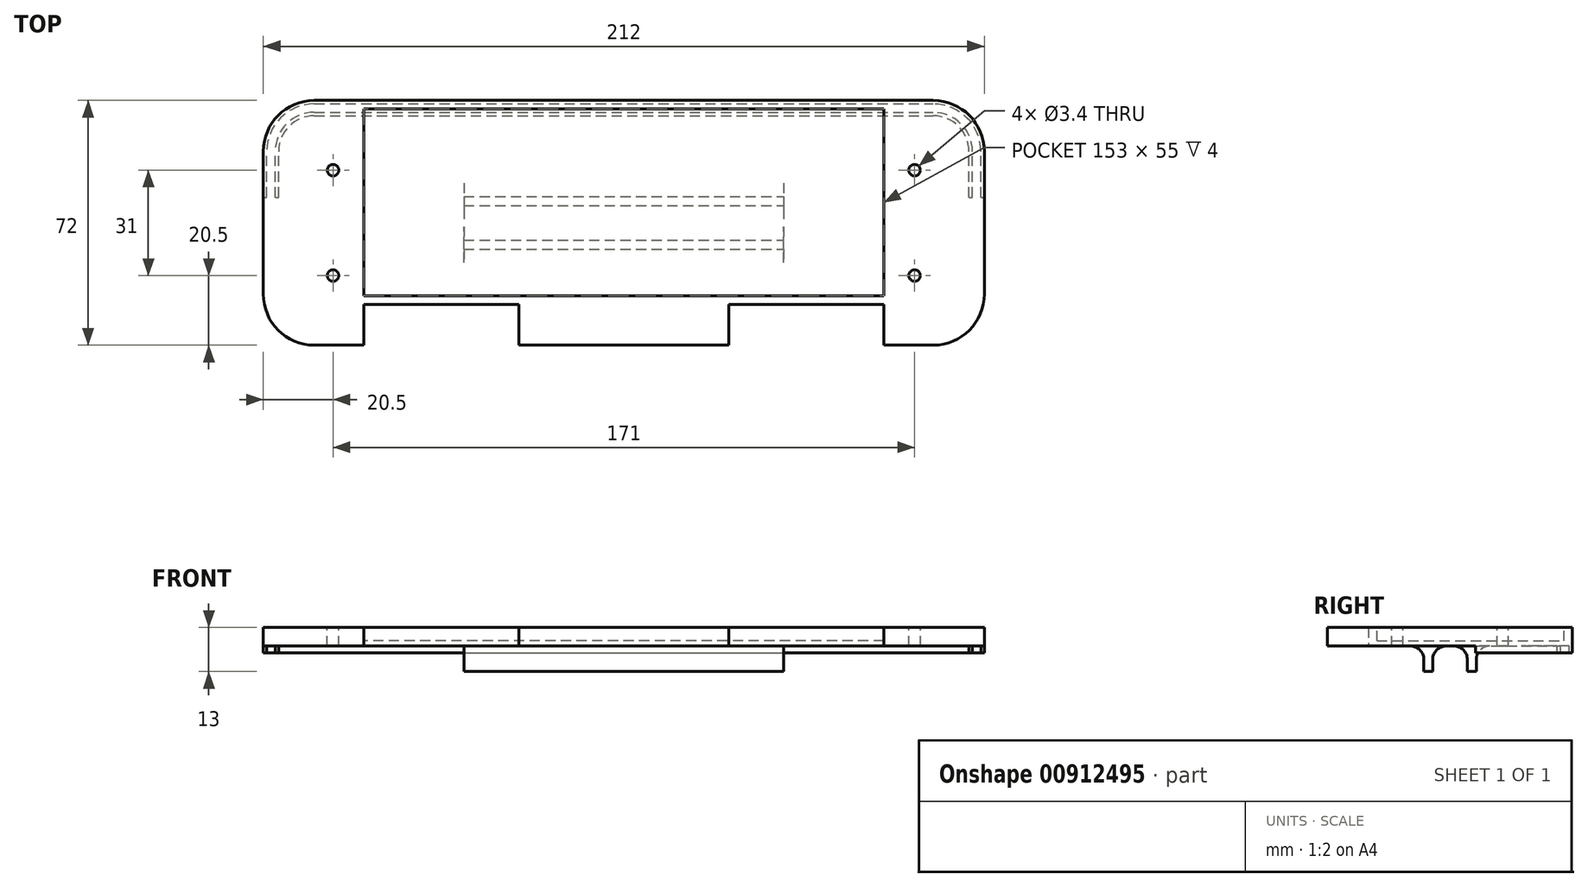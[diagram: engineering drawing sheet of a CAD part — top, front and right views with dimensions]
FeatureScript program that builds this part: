
annotation { "Feature Type Name" : "Feature", "Feature Type Description" : "" }
export const myFeature = defineFeature(function(context is Context, id is Id, definition is map)
    precondition{}
    {
        {
            var Q0;
            Q0=qCreatedBy(makeId("Top.planeOp"),FACE);
            var sketch = newSketch(context, id + "F0", { "sketchPlane" : qUnion([Q0])});
            skLineSegment(sketch, "E0.bottom", {"start": v(-106, 36) * mm, "end": v(106, 36) * mm});
            skLineSegment(sketch, "E0.top", {"start": v(-106, -36) * mm, "end": v(106, -36) * mm});
            skLineSegment(sketch, "E0.left", {"start": v(-106, 36) * mm, "end": v(-106, -36) * mm});
            skLineSegment(sketch, "E0.right", {"start": v(106, 36) * mm, "end": v(106, -36) * mm});
            skPoint(sketch, "E0.middle", {"position": v(0, 0) * mm});
            skSolve(sketch);
        }
        {
            var Q0;
            Q0=qSketchRegion(id+"F0",true);
            extrude(context, id + "F1", {"entities" : qUnion([Q0]), "depth" : 5.5 * mm, "offsetDistance" : 25 * mm});
        }
        {
            var Q0;
            Q0=makeQuery(id+"F1.opExtrude","SWEPT_EDGE",EDGE,{"disambiguationData":[OSD([sQuery(id+"F0.wireOp",EDGE,"E0.top"),sQuery(id+"F0.wireOp",EDGE,"E0.left")])]});
            var Q1;
            Q1=makeQuery(id+"F1.opExtrude","SWEPT_EDGE",EDGE,{"disambiguationData":[OSD([sQuery(id+"F0.wireOp",EDGE,"E0.top"),sQuery(id+"F0.wireOp",EDGE,"E0.right")])]});
            fillet(context, id + "F2", {"entities" : qUnion([Q0, Q1]), "radius" : 15 * mm, "tangentPropagation" : true, "allowEdgeOverflow" : false});
        }
        {
            var Q0;
            Q0=makeQuery(id+"F1.opExtrude","SWEPT_FACE",FACE,{"disambiguationData":[OSD([sQuery(id+"F0.wireOp",EDGE,"E0.top")])]});
            var sketch = newSketch(context, id + "F3", { "sketchPlane" : qUnion([Q0])});
            skLineSegment(sketch, "E1.bottom", {"start": v(-76.5, 5.5) * mm, "end": v(-30.88, 5.5) * mm});
            skLineSegment(sketch, "E1.top", {"start": v(-76.5, 0) * mm, "end": v(-30.88, 0) * mm});
            skLineSegment(sketch, "E1.left", {"start": v(-76.5, 5.5) * mm, "end": v(-76.5, 0) * mm});
            skLineSegment(sketch, "E1.right", {"start": v(-30.88, 5.5) * mm, "end": v(-30.88, 0) * mm});
            skLineSegment(sketch, "E2.bottom", {"start": v(30.88, 5.5) * mm, "end": v(76.5, 5.5) * mm});
            skLineSegment(sketch, "E2.top", {"start": v(30.88, 0) * mm, "end": v(76.5, 0) * mm});
            skLineSegment(sketch, "E2.left", {"start": v(30.88, 5.5) * mm, "end": v(30.88, 0) * mm});
            skLineSegment(sketch, "E2.right", {"start": v(76.5, 5.5) * mm, "end": v(76.5, 0) * mm});
            skSolve(sketch);
        }
        {
            var Q0;
            Q0=qSketchRegion(id+"F3",true);
            extrude(context, id + "F4", {"entities" : qUnion([Q0]), "operationType" : NewBodyOperationType.REMOVE, "oppositeDirection" : true, "depth" : 12 * mm, "offsetDistance" : 25 * mm});
        }
        {
            var Q0;
            Q0=makeQuery(id+"F1.opExtrude","CAP_FACE",FACE,{"disambiguationData":[OSD([sQuery(id+"F0.wireOp",EDGE,"E0.bottom"),sQuery(id+"F0.wireOp",EDGE,"E0.top"),sQuery(id+"F0.wireOp",EDGE,"E0.left"),sQuery(id+"F0.wireOp",EDGE,"E0.right")])],"isStart":true});
            var sketch = newSketch(context, id + "F5", { "sketchPlane" : qUnion([Q0])});
            skLineSegment(sketch, "E3.bottom", {"start": v(-106, -7.5) * mm, "end": v(-105, -7.5) * mm});
            skLineSegment(sketch, "E3.top", {"start": v(-106, -36) * mm, "end": v(106, -36) * mm});
            skLineSegment(sketch, "E3.left", {"start": v(-106, -7.5) * mm, "end": v(-106, -36) * mm});
            skLineSegment(sketch, "E3.right", {"start": v(106, -7.5) * mm, "end": v(106, -36) * mm});
            skLineSegment(sketch, "E4.top", {"start": v(-101.5, -31.5) * mm, "end": v(101.5, -31.5) * mm});
            skLineSegment(sketch, "E4.left", {"start": v(-101.5, -7.5) * mm, "end": v(-101.5, -31.5) * mm});
            skLineSegment(sketch, "E4.right", {"start": v(101.5, -7.5) * mm, "end": v(101.5, -31.5) * mm});
            skLineSegment(sketch, "E5.trimOffspring", {"start": v(101.5, -7.5) * mm, "end": v(102.5, -7.5) * mm});
            skLineSegment(sketch, "E6.bottom", {"start": v(-102.5, -7.5) * mm, "end": v(-101.5, -7.5) * mm});
            skLineSegment(sketch, "E6.top", {"start": v(-105, -35) * mm, "end": v(105, -35) * mm});
            skLineSegment(sketch, "E6.left", {"start": v(-105, -7.5) * mm, "end": v(-105, -35) * mm});
            skLineSegment(sketch, "E6.right", {"start": v(105, -7.5) * mm, "end": v(105, -35) * mm});
            skLineSegment(sketch, "E7.top", {"start": v(-102.5, -32.5) * mm, "end": v(102.5, -32.5) * mm});
            skLineSegment(sketch, "E7.left", {"start": v(-102.5, -7.5) * mm, "end": v(-102.5, -32.5) * mm});
            skLineSegment(sketch, "E7.right", {"start": v(102.5, -7.5) * mm, "end": v(102.5, -32.5) * mm});
            skLineSegment(sketch, "E8.trimOffspring", {"start": v(105, -7.5) * mm, "end": v(106, -7.5) * mm});
            skSolve(sketch);
        }
        {
            var Q0;
            Q0=qSketchRegion(id+"F5",true);
            extrude(context, id + "F6", {"entities" : qUnion([Q0]), "operationType" : NewBodyOperationType.ADD, "depth" : 2 * mm, "offsetDistance" : 25 * mm});
        }
        {
            var Q0;
            Q0=makeQuery(id+"F6.opExtrude","SWEPT_EDGE",EDGE,{"disambiguationData":[OSD([sQuery(id+"F5.wireOp",EDGE,"E4.top"),sQuery(id+"F5.wireOp",EDGE,"E4.right")])]});
            var Q1;
            Q1=makeQuery(id+"F6.opExtrude","SWEPT_EDGE",EDGE,{"disambiguationData":[OSD([sQuery(id+"F5.wireOp",EDGE,"E4.top"),sQuery(id+"F5.wireOp",EDGE,"E4.left")])]});
            fillet(context, id + "F7", {"entities" : qUnion([Q0, Q1]), "radius" : 10.5 * mm, "tangentPropagation" : true, "allowEdgeOverflow" : false});
        }
        {
            var Q0;
            Q0=makeQuery(id+"F6.opExtrude","SWEPT_EDGE",EDGE,{"disambiguationData":[OSD([sQuery(id+"F5.wireOp",EDGE,"E7.top"),sQuery(id+"F5.wireOp",EDGE,"E7.right")])]});
            var Q1;
            Q1=makeQuery(id+"F6.opExtrude","SWEPT_EDGE",EDGE,{"disambiguationData":[OSD([sQuery(id+"F5.wireOp",EDGE,"E7.top"),sQuery(id+"F5.wireOp",EDGE,"E7.left")])]});
            fillet(context, id + "F8", {"entities" : qUnion([Q0, Q1]), "radius" : 11.5 * mm, "tangentPropagation" : true, "allowEdgeOverflow" : false});
        }
        {
            var Q0;
            Q0=makeQuery(id+"F6.opExtrude","SWEPT_EDGE",EDGE,{"disambiguationData":[OSD([sQuery(id+"F5.wireOp",EDGE,"E6.top"),sQuery(id+"F5.wireOp",EDGE,"E6.right")])]});
            var Q1;
            Q1=makeQuery(id+"F6.opExtrude","SWEPT_EDGE",EDGE,{"disambiguationData":[OSD([sQuery(id+"F5.wireOp",EDGE,"E6.top"),sQuery(id+"F5.wireOp",EDGE,"E6.left")])]});
            fillet(context, id + "F9", {"entities" : qUnion([Q0, Q1]), "radius" : 14 * mm, "tangentPropagation" : true, "allowEdgeOverflow" : false});
        }
        {
            var Q0;
            Q0=makeQuery(id+"F6.boolean.opBoolean","MERGE",EDGE,{"derivedFrom":[makeQuery(id+"F1.opExtrude","SWEPT_EDGE",EDGE,{"disambiguationData":[OSD([sQuery(id+"F0.wireOp",EDGE,"E0.bottom"),sQuery(id+"F0.wireOp",EDGE,"E0.right")])]}),makeQuery(id+"F6.opExtrude","SWEPT_EDGE",EDGE,{"disambiguationData":[OSD([sQuery(id+"F5.wireOp",EDGE,"E3.top"),sQuery(id+"F5.wireOp",EDGE,"E3.right")])]})]});
            var Q1;
            Q1=makeQuery(id+"F6.boolean.opBoolean","MERGE",EDGE,{"derivedFrom":[makeQuery(id+"F1.opExtrude","SWEPT_EDGE",EDGE,{"disambiguationData":[OSD([sQuery(id+"F0.wireOp",EDGE,"E0.bottom"),sQuery(id+"F0.wireOp",EDGE,"E0.left")])]}),makeQuery(id+"F6.opExtrude","SWEPT_EDGE",EDGE,{"disambiguationData":[OSD([sQuery(id+"F5.wireOp",EDGE,"E3.top"),sQuery(id+"F5.wireOp",EDGE,"E3.left")])]})]});
            fillet(context, id + "F10", {"entities" : qUnion([Q0, Q1]), "radius" : 15 * mm, "tangentPropagation" : true, "allowEdgeOverflow" : false});
        }
        {
            var Q0;
            Q0=makeQuery(id+"F1.opExtrude","CAP_FACE",FACE,{"disambiguationData":[OSD([sQuery(id+"F0.wireOp",EDGE,"E0.bottom"),sQuery(id+"F0.wireOp",EDGE,"E0.top"),sQuery(id+"F0.wireOp",EDGE,"E0.left"),sQuery(id+"F0.wireOp",EDGE,"E0.right")])],"isStart":false});
            var sketch = newSketch(context, id + "F11", { "sketchPlane" : qUnion([Q0])});
            skLineSegment(sketch, "E9.bottom", {"start": v(76.5, 33.5) * mm, "end": v(-76.5, 33.5) * mm});
            skLineSegment(sketch, "E9.top", {"start": v(76.5, -21.5) * mm, "end": v(-76.5, -21.5) * mm});
            skLineSegment(sketch, "E9.left", {"start": v(76.5, -21.5) * mm, "end": v(76.5, 33.5) * mm});
            skLineSegment(sketch, "E9.right", {"start": v(-76.5, -21.5) * mm, "end": v(-76.5, 33.5) * mm});
            skPoint(sketch, "E9.middle", {"position": v(0, 0) * mm});
            skSolve(sketch);
        }
        {
            var Q0;
            Q0=qSketchRegion(id+"F11",true);
            extrude(context, id + "F12", {"entities" : qUnion([Q0]), "operationType" : NewBodyOperationType.REMOVE, "oppositeDirection" : true, "depth" : 4 * mm, "offsetDistance" : 25 * mm});
        }
        {
            var Q0;
            Q0=makeQuery(id+"F1.opExtrude","CAP_FACE",FACE,{"disambiguationData":[OSD([sQuery(id+"F0.wireOp",EDGE,"E0.bottom"),sQuery(id+"F0.wireOp",EDGE,"E0.top"),sQuery(id+"F0.wireOp",EDGE,"E0.left"),sQuery(id+"F0.wireOp",EDGE,"E0.right")])],"isStart":false});
            var sketch = newSketch(context, id + "F13", { "sketchPlane" : qUnion([Q0])});
            skPoint(sketch, "E10", {"position": v(85.5, 15.5) * mm});
            skPoint(sketch, "E11", {"position": v(85.5, -15.5) * mm});
            skPoint(sketch, "E12", {"position": v(-85.5, 15.5) * mm});
            skPoint(sketch, "E13", {"position": v(-85.5, -15.5) * mm});
            skSolve(sketch);
        }
        {
            var Q0;
            Q0=sQuery(id+"F13.wireOp",VERTEX,"E12");
            var Q1;
            Q1=sQuery(id+"F13.wireOp",VERTEX,"5491ae01-6f72-4d20-b0d5-79ec1aa562b5");
            var Q2;
            Q2=sQuery(id+"F13.wireOp",VERTEX,"E10");
            var Q3;
            Q3=sQuery(id+"F13.wireOp",VERTEX,"E11");
            var Q4;
            Q4=sQuery(id+"F13.wireOp",VERTEX,"E13");
            var Q5;
            Q5=makeQuery(id+"F1.opExtrude","SWEPT_BODY",BODY,{"disambiguationData":[OSD([sQuery(id+"F0.wireOp",EDGE,"E0.bottom"),sQuery(id+"F0.wireOp",EDGE,"E0.top"),sQuery(id+"F0.wireOp",EDGE,"E0.left"),sQuery(id+"F0.wireOp",EDGE,"E0.right")])]});
            hole(context, id + "F14", {"style" : HoleStyle.SIMPLE, "endStyle" : HoleEndStyle.THROUGH, "standardTappedOrClearance" : lookupTablePath({ "fit" : "Normal", "standard" : "ISO", "size" : "M3", "type" : "Clearance" }), "standardBlindInLast" : lookupTablePath({ "fit" : "Normal", "standard" : "ISO", "size" : "M3", "type" : "Clearance" }), "holeDiameter" : 3.4 * mm, "majorDiameter" : 5 * mm, "isTappedThrough" : true, "tappedDepth" : 12 * mm, "tapClearance" : 3, "locations" : qUnion([Q0, Q1, Q2, Q3, Q4]), "scope" : qUnion([Q5])});
        }
        {
            var Q0;
            Q0=makeQuery(id+"F1.opExtrude","CAP_FACE",FACE,{"disambiguationData":[OSD([sQuery(id+"F0.wireOp",EDGE,"E0.bottom"),sQuery(id+"F0.wireOp",EDGE,"E0.top"),sQuery(id+"F0.wireOp",EDGE,"E0.left"),sQuery(id+"F0.wireOp",EDGE,"E0.right")])],"isStart":true});
            var sketch = newSketch(context, id + "F15", { "sketchPlane" : qUnion([Q0])});
            skLineSegment(sketch, "E14.bottom", {"start": v(-47, 11.7) * mm, "end": v(47, 11.7) * mm});
            skLineSegment(sketch, "E14.top", {"start": v(-47, 1.1) * mm, "end": v(47, 1.1) * mm});
            skLineSegment(sketch, "E14.left", {"start": v(-47, 11.7) * mm, "end": v(-47, 1.1) * mm});
            skLineSegment(sketch, "E14.right", {"start": v(47, 11.7) * mm, "end": v(47, 1.1) * mm});
            skPoint(sketch, "E14.middle", {"position": v(0, 6.4) * mm});
            skLineSegment(sketch, "E15.bottom", {"start": v(-47, -11.7) * mm, "end": v(47, -11.7) * mm});
            skLineSegment(sketch, "E15.top", {"start": v(-47, -1.1) * mm, "end": v(47, -1.1) * mm});
            skLineSegment(sketch, "E15.left", {"start": v(-47, -11.7) * mm, "end": v(-47, -1.1) * mm});
            skLineSegment(sketch, "E15.right", {"start": v(47, -11.7) * mm, "end": v(47, -1.1) * mm});
            skPoint(sketch, "E15.middle", {"position": v(0, -6.4) * mm});
            skSolve(sketch);
        }
        {
            var Q0;
            Q0 = qSketchRegion(id + "F15", true);
            extrude(context, id + "F16", {"entities" : qUnion([Q0]), "operationType" : NewBodyOperationType.ADD, "depth" : 7.5 * mm, "offsetDistance" : 25 * mm});
        }
        {
            var Q0;
            Q0=makeQuery(id+"F16.opExtrude","SWEPT_FACE",FACE,{"disambiguationData":[OSD([sQuery(id+"F15.wireOp",EDGE,"E15.right")])]});
            var sketch = newSketch(context, id + "F17", { "sketchPlane" : qUnion([Q0])});
            skArc(sketch, "E16", {"start": v(11.7, 0) * mm, "mid": v(8.87, -1.17) * mm, "end": v(7.7, -4) * mm});
            skLineSegment(sketch, "E17.top", {"start": v(11.7, -7.5) * mm, "end": v(7.7, -7.5) * mm});
            skLineSegment(sketch, "E17.left", {"start": v(11.7, 0) * mm, "end": v(11.7, -7.5) * mm});
            skLineSegment(sketch, "E17.right", {"start": v(7.7, -4) * mm, "end": v(7.7, -7.5) * mm});
            skArc(sketch, "E18", {"start": v(-1.1, 0) * mm, "mid": v(-3.92, -1.17) * mm, "end": v(-5.1, -4) * mm});
            skLineSegment(sketch, "E19.top", {"start": v(-1.1, -7.5) * mm, "end": v(-5.1, -7.5) * mm});
            skLineSegment(sketch, "E19.left", {"start": v(-1.1, 0) * mm, "end": v(-1.1, -7.5) * mm});
            skLineSegment(sketch, "E19.right", {"start": v(-5.1, -4) * mm, "end": v(-5.1, -7.5) * mm});
            skArc(sketch, "E20", {"start": v(5.1, -4) * mm, "mid": v(3.92, -1.17) * mm, "end": v(1.1, 0) * mm});
            skLineSegment(sketch, "E21.top", {"start": v(1.1, -7.5) * mm, "end": v(5.1, -7.5) * mm});
            skLineSegment(sketch, "E21.right", {"start": v(5.1, -4) * mm, "end": v(5.1, -7.5) * mm});
            skLineSegment(sketch, "E22", {"start": v(1.1, 0) * mm, "end": v(1.1, -7.5) * mm});
            skArc(sketch, "E23", {"start": v(-7.7, -4) * mm, "mid": v(-8.87, -1.17) * mm, "end": v(-11.7, 0) * mm});
            skLineSegment(sketch, "E24.top", {"start": v(-11.7, -7.5) * mm, "end": v(-7.7, -7.5) * mm});
            skLineSegment(sketch, "E24.right", {"start": v(-7.7, -4) * mm, "end": v(-7.7, -7.5) * mm});
            skLineSegment(sketch, "E25", {"start": v(-11.7, 0) * mm, "end": v(-11.7, -7.5) * mm});
            skSolve(sketch);
        }
        {
            var Q0;
            Q0 = qSketchRegion(id + "F17", true);
            extrude(context, id + "F18", {"entities" : qUnion([Q0]), "operationType" : NewBodyOperationType.REMOVE, "oppositeDirection" : true, "depth" : 94 * mm, "offsetDistance" : 25 * mm});
        }
    });
